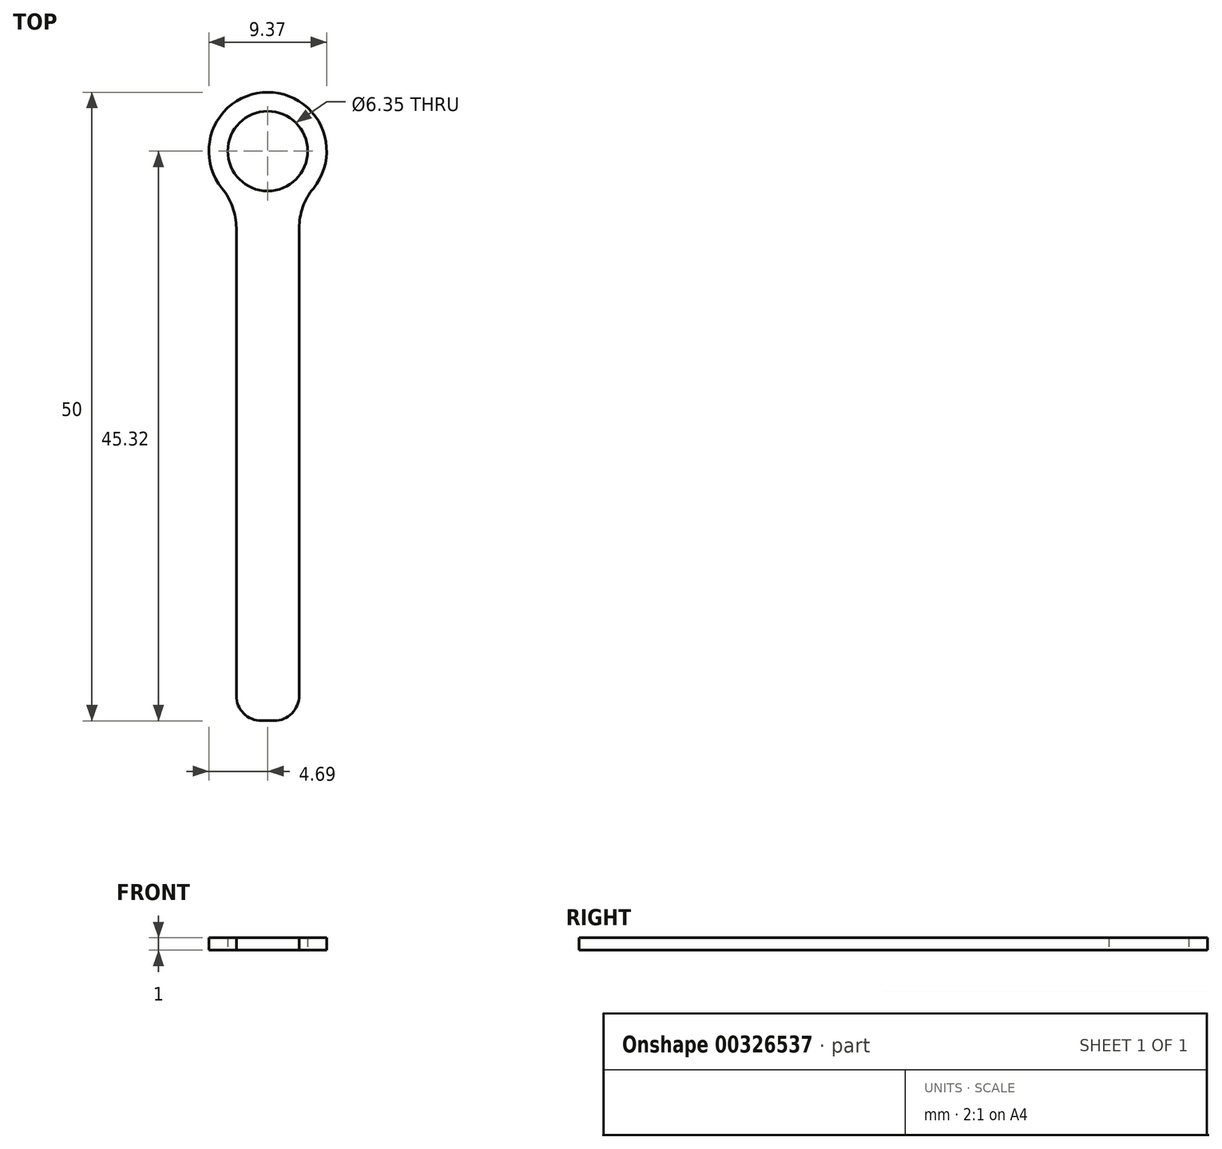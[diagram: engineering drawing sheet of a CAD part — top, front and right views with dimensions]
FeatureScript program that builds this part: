
annotation { "Feature Type Name" : "Feature", "Feature Type Description" : "" }
export const myFeature = defineFeature(function(context is Context, id is Id, definition is map)
    precondition{}
    {
        {
            var Q0;
            Q0=qCreatedBy(makeId("Top.planeOp"),FACE);
            var sketch = newSketch(context, id + "F0", { "sketchPlane" : qUnion([Q0])});
            skArc(sketch, "E0", {"start": v(3.63, -2.96) * mm, "mid": v(0, 4.68) * mm, "end": v(-3.63, -2.96) * mm});
            skCircle(sketch, "E1", {"center": v(0, 0) * mm, "radius": 3.17 * mm});
            skLineSegment(sketch, "E2.top", {"start": v(0.5, -45.31) * mm, "end": v(-0.5, -45.31) * mm});
            skPoint(sketch, "E2.middle", {"position": v(0, -35.75) * mm});
            skLineSegment(sketch, "E3.trimOffspring", {"start": v(-2.5, -6.13) * mm, "end": v(-2.5, -43.31) * mm});
            skLineSegment(sketch, "E4.trimOffspring", {"start": v(2.5, -6.13) * mm, "end": v(2.5, -43.31) * mm});
            skPoint(sketch, "E2.bottom.start.orphan", {"position": v(2.5, -26.18) * mm});
            skPoint(sketch, "E2.right.start.orphan", {"position": v(-2.5, -26.18) * mm});
            skPoint(sketch, "E5.visualSharp", {"position": v(-2.5, -3.96) * mm});
            skArc(sketch, "E5.filletArc", {"start": v(-2.5, -6.13) * mm, "mid": v(-2.8, -4.45) * mm, "end": v(-3.63, -2.96) * mm});
            skPoint(sketch, "E6.visualSharp", {"position": v(2.5, -3.96) * mm});
            skArc(sketch, "E6.filletArc", {"start": v(3.63, -2.96) * mm, "mid": v(2.8, -4.45) * mm, "end": v(2.5, -6.13) * mm});
            skLineSegment(sketch, "E7", {"start": v(0, 4.68) * mm, "end": v(8.76, 4.68) * mm, "construction": true});
            skPoint(sketch, "E8.visualSharp", {"position": v(-2.5, -45.31) * mm});
            skArc(sketch, "E8.filletArc", {"start": v(-2.5, -43.31) * mm, "mid": v(-1.91, -44.73) * mm, "end": v(-0.5, -45.31) * mm});
            skPoint(sketch, "E9.visualSharp", {"position": v(2.5, -45.31) * mm});
            skArc(sketch, "E9.filletArc", {"start": v(0.5, -45.31) * mm, "mid": v(1.91, -44.73) * mm, "end": v(2.5, -43.31) * mm});
            skSolve(sketch);
        }
        {
            var Q0;
            Q0 = qSketchRegion(id + "F0", true);
            extrude(context, id + "F1", {"entities" : qUnion([Q0]), "depth" : 1 * mm});
        }
    });
